FCSTD DOCUMENT  (FreeCAD 0.21R33771 (Git))
Label: Fiber_mount_assembly_Montana
License: All rights reserved
LicenseURL: https://en.wikipedia.org/wiki/All_rights_reserved
objects: App::Link×9, App::DocumentObjectGroup×2, PartDesign::CoordinateSystem×1, App::FeaturePython×1, App::Part×1
note: 1 computed .brp shape members not serialized (recipe doc carries the construction recipe); baked Part::Feature solids carry a one-line shape summary decoded from their .brp
EXTERNAL_REF file=../Optomecanics/Cage.FCStd obj=HoleAxis_1
EXTERNAL_REF file=Fiber_buffer_montana.FCStd obj=Top_center
EXTERNAL_REF file=../Optomecanics/Cage.FCStd obj=Assembly
EXTERNAL_REF file=../Optomecanics/Cage.FCStd obj=HoleAxis_3
EXTERNAL_REF file=../Optomecanics/Cage_rods.FCStd obj=HoleAxis_1
EXTERNAL_REF file=../Optomecanics/Cage_rods.FCStd obj=Assembly
EXTERNAL_REF file=../Optomecanics/Cage.FCStd obj=HoleAxis_4
EXTERNAL_REF file=../Optomecanics/Cage.FCStd obj=HoleAxis_5
EXTERNAL_REF file=../Optomecanics/Cage.FCStd obj=HoleAxis_6
EXTERNAL_REF file=../Optomecanics/Cage.FCStd obj=HoleAxis_2
EXTERNAL_REF file=SMA_port.FCStd obj=HoleAxis_1
EXTERNAL_REF file=SMA_port.FCStd obj=Assembly
EXTERNAL_REF file=Fiber_buffer_montana.FCStd obj=Bottom_center
EXTERNAL_REF file=../Optomecanics/Post_4inches.FCStd obj=HoleAxis_2
EXTERNAL_REF file=Fiber_buffer_montana.FCStd obj=Assembly
EXTERNAL_REF file=../Optomecanics/Post_4inches.FCStd obj=HoleAxis_1
EXTERNAL_REF file=../Optomecanics/Post_4inches.FCStd obj=Assembly

FEATURE [PartDesign::CoordinateSystem] LCS_Origin
  AttacherType = Attacher::AttachEngine3D
  MapMode = 2
  Support = -> [X_Axis]
FEATURE [App::DocumentObjectGroup] Constraints
FEATURE [App::FeaturePython] Variables  # WARN: FeaturePython — macro-defined, semantics opaque (R4)
  Type = App::PropertyContainer
FEATURE [App::DocumentObjectGroup] Configurations
FEATURE [App::Link] Cage
  AttachedBy = #HoleAxis_1
  AttachedTo = Fiber_buffer_montana#Top_center
  LinkPlacement = pos=(-1.35e-14,9.8e-15,141.92) rot=(0.57735,0.57735,0.57735;2.0944rad)
  LinkedObject = -> <external ../Optomecanics/Cage.FCStd>#Assembly
  Placement = pos=(-1.35e-14,9.8e-15,141.92) rot=(0.57735,0.57735,0.57735;2.0944rad)
  SolverId = Asm4EE
  expr: Placement = Fiber_buffer_montana.Placement * Fiber_buffer_montana#Top_center.Placement * AttachmentOffset * Cage#HoleAxis_1.Placement ^ -1
FEATURE [App::Link] Cage_rods  label="Cage_rod1"
  AttachedBy = #HoleAxis_1
  AttachedTo = Cage#HoleAxis_3
  AttachmentOffset = pos=(0,0,5) rot=(0,1,0;3.14159rad)
  LinkPlacement = pos=(20.527,-15,156.92) rot=(0.022572,-0.99949,-0.022572;1.57131rad)
  LinkedObject = -> <external ../Optomecanics/Cage_rods.FCStd>#Assembly
  Placement = pos=(20.527,-15,156.92) rot=(0.022572,-0.99949,-0.022572;1.57131rad)
  SolverId = Asm4EE
  expr: Placement = Cage.Placement * Cage#HoleAxis_3.Placement * AttachmentOffset * Cage_rods#HoleAxis_1.Placement ^ -1
FEATURE [App::Link] Cage_rods001  label="Cage_rod2"
  AttachedBy = #HoleAxis_1
  AttachedTo = Cage#HoleAxis_4
  AttachmentOffset = pos=(0,0,5) rot=(0,1,0;3.14159rad)
  LinkPlacement = pos=(20.527,15,156.92) rot=(0.022572,-0.99949,-0.022572;1.57131rad)
  LinkedObject = -> <external ../Optomecanics/Cage_rods.FCStd>#Assembly
  Placement = pos=(20.527,15,156.92) rot=(0.022572,-0.99949,-0.022572;1.57131rad)
  SolverId = Asm4EE
  expr: Placement = Cage.Placement * Cage#HoleAxis_4.Placement * AttachmentOffset * Cage_rods#HoleAxis_1.Placement ^ -1
FEATURE [App::Link] Cage_rods002  label="Cage_rod3"
  AttachedBy = #HoleAxis_1
  AttachedTo = Cage#HoleAxis_5
  AttachmentOffset = pos=(0,0,5) rot=(0,1,0;3.14159rad)
  LinkPlacement = pos=(20.527,-15,126.92) rot=(0.022572,-0.99949,-0.022572;1.57131rad)
  LinkedObject = -> <external ../Optomecanics/Cage_rods.FCStd>#Assembly
  Placement = pos=(20.527,-15,126.92) rot=(0.022572,-0.99949,-0.022572;1.57131rad)
  SolverId = Asm4EE
  expr: Placement = Cage.Placement * Cage#HoleAxis_5.Placement * AttachmentOffset * Cage_rods#HoleAxis_1.Placement ^ -1
FEATURE [App::Link] Cage_rods003  label="Cage_rod4"
  AttachedBy = #HoleAxis_1
  AttachedTo = Cage#HoleAxis_6
  AttachmentOffset = pos=(0,0,5) rot=(0.707107,0.707107,0;3.14159rad)
  LinkPlacement = pos=(20.527,15,126.92) rot=(0.585847,-0.55997,-0.585847;2.12066rad)
  LinkedObject = -> <external ../Optomecanics/Cage_rods.FCStd>#Assembly
  Placement = pos=(20.527,15,126.92) rot=(0.585847,-0.55997,-0.585847;2.12066rad)
  SolverId = Asm4EE
  expr: Placement = Cage.Placement * Cage#HoleAxis_6.Placement * AttachmentOffset * Cage_rods#HoleAxis_1.Placement ^ -1
FEATURE [App::Link] Cage001
  AttachedBy = #HoleAxis_2
  AttachedTo = Cage#HoleAxis_2
  AttachmentOffset = pos=(0,0,-35) rot=(0,0,1;0rad)
  LinkPlacement = pos=(35,-4.1e-15,141.92) rot=(0.57735,0.57735,0.57735;2.0944rad)
  LinkedObject = -> <external ../Optomecanics/Cage.FCStd>#Assembly
  Placement = pos=(35,-4.1e-15,141.92) rot=(0.57735,0.57735,0.57735;2.0944rad)
  SolverId = Asm4EE
  expr: Placement = Cage.Placement * Cage#HoleAxis_2.Placement * AttachmentOffset * Cage#HoleAxis_2.Placement ^ -1
FEATURE [App::Link] SMA_port
  AttachedBy = #HoleAxis_1
  AttachedTo = Cage001#HoleAxis_2
  AttachmentOffset = pos=(0,0,3) rot=(0,1,0;3.14159rad)
  LinkPlacement = pos=(39.62,-4.51e-14,141.92) rot=(1,0,0;4.71239rad)
  LinkedObject = -> <external SMA_port.FCStd>#Assembly
  Placement = pos=(39.62,-4.51e-14,141.92) rot=(1,0,0;4.71239rad)
  SolverId = Asm4EE
  expr: Placement = Cage001.Placement * Cage#HoleAxis_2.Placement * AttachmentOffset * SMA_port#HoleAxis_1.Placement ^ -1
FEATURE [App::Link] Fiber_buffer_montana
  AttachedBy = #Bottom_center
  AttachedTo = Post_4inches#HoleAxis_2
  LinkPlacement = pos=(-8.1e-15,5.7e-15,101.6) rot=(0,0,1;0rad)
  LinkedObject = -> <external Fiber_buffer_montana.FCStd>#Assembly
  Placement = pos=(-8.1e-15,5.7e-15,101.6) rot=(0,0,1;0rad)
  SolverId = Asm4EE
  expr: Placement = Post_4inches.Placement * Post_4inches#HoleAxis_2.Placement * AttachmentOffset * Fiber_buffer_montana#Bottom_center.Placement ^ -1
FEATURE [App::Link] Post_4inches
  AttachedBy = #HoleAxis_1
  AttachedTo = Parent Assembly#LCS_Origin
  LinkPlacement = pos=(-5.3e-15,-1.07e-14,50.8) rot=(0.57735,0.57735,0.57735;2.0944rad)
  LinkedObject = -> <external ../Optomecanics/Post_4inches.FCStd>#Assembly
  Placement = pos=(-5.3e-15,-1.07e-14,50.8) rot=(0.57735,0.57735,0.57735;2.0944rad)
  SolverId = Asm4EE
  expr: Placement = LCS_Origin.Placement * AttachmentOffset * Post_4inches#HoleAxis_1.Placement ^ -1
FEATURE [App::Part] Assembly
  AssemblyType = Part::Link
  Group = -> [LCS_Origin,Constraints,Variables,Configurations,Cage,Cage_rods,Cage_rods001,Cage_rods002,Cage_rods003,Cage001,SMA_port,Fiber_buffer_montana,Post_4inches]
  Origin = -> Origin
  Type = Assembly

RESOLVED EXTERNAL PARTS (link-assembly join: the EXTERNAL_REF files above that resolve inside this repo's crawl, each included once):
---- part Fiber_buffer_montana.FCStd = doc fcstd_8a898043692d ----
FCSTD DOCUMENT  (FreeCAD 0.21R33771 (Git))
Label: Fiber_buffer_montana
License: All rights reserved
LicenseURL: https://en.wikipedia.org/wiki/All_rights_reserved
objects: Sketcher::SketchObject×2, App::DocumentObjectGroup×2, PartDesign::CoordinateSystem×2, PartDesign::Pad×1, PartDesign::Hole×1, PartDesign::Body×1, App::FeaturePython×1, App::Part×1
note: 9 computed .brp shape members not serialized (recipe doc carries the construction recipe); baked Part::Feature solids carry a one-line shape summary decoded from their .brp

FEATURE [Sketcher::SketchObject] Sketch
  FullyConstrained = true
  MapMode = 5
  Support = -> [XY_Plane]
  sketch-geometry (4):
    g0: LineSegment StartX=-12.7 StartY=12.7 StartZ=0 EndX=12.7 EndY=12.7 EndZ=0
    g1: LineSegment StartX=12.7 StartY=12.7 StartZ=0 EndX=12.7 EndY=-12.7 EndZ=0
    g2: LineSegment StartX=12.7 StartY=-12.7 StartZ=0 EndX=-12.7 EndY=-12.7 EndZ=0
    g3: LineSegment StartX=-12.7 StartY=-12.7 StartZ=0 EndX=-12.7 EndY=12.7 EndZ=0
  constraints (12):
    c: Coincident(g0,g1)
    c: Coincident(g1,g2)
    c: Coincident(g2,g3)
    c: Coincident(g3,g0)
    c: Horizontal(g0)
    c: Horizontal(g2)
    c: Vertical(g1)
    c: Vertical(g3)
    c: DistanceX(g0,g-1) = 12.7
    c: DistanceX(g0,g0) = 25.4
    c: DistanceY(g1,g1) = 25.4
    c: DistanceY(g1,g-1) = 12.7
FEATURE [PartDesign::Pad] Pad
  Direction = (0,0,1)
  Length = 20
  Length2 = 10
  Profile = -> Sketch
  ReferenceAxis = -> Sketch [N_Axis]
  Type = 0
FEATURE [Sketcher::SketchObject] Sketch001
  FullyConstrained = true
  MapMode = 5
  Placement = pos=(0,0,20) rot=(0,0,1;0rad)
  Support = -> [Pad]
  sketch-geometry (1):
    g0: Circle CenterX=0 CenterY=0 CenterZ=0 NormalX=0 NormalY=0 NormalZ=1 AngleXU=0 Radius=1.5875
  constraints (2):
    c: Coincident(g0,g-1)
    c: Diameter(g0) = 3.175
FEATURE [PartDesign::Hole] Hole
  BaseFeature = -> Pad
  CustomThreadClearance = 0
  Depth = 75.3197
  DepthType = 1
  Diameter = 3.17
  DrillForDepth = false
  DrillPoint = 1
  DrillPointAngle = 118
  HoleCutCountersinkAngle = 90
  HoleCutCustomValues = false
  HoleCutDepth = 0
  HoleCutDiameter = 6.1
  HoleCutType = 0
  ModelThread = false
  Profile = -> Sketch001
  Tapered = false
  TaperedAngle = 90
  ThreadClass = 0
  ThreadDepth = 75.3197
  ThreadDepthType = 0
  ThreadDirection = 0
  ThreadFit = 0
  ThreadSize = 0
  ThreadType = 0
  Threaded = false
  UseCustomThreadClearance = false
FEATURE [PartDesign::Body] Body
  Group = -> [Sketch,Pad,Sketch001,Hole]
  Origin = -> Origin
  Tip = -> Hole
FEATURE [App::DocumentObjectGroup] Constraints
FEATURE [App::FeaturePython] Variables  # WARN: FeaturePython — macro-defined, semantics opaque (R4)
  Type = App::PropertyContainer
FEATURE [App::DocumentObjectGroup] Configurations
FEATURE [PartDesign::CoordinateSystem] Bottom_center
  AttacherType = Attacher::AttachEngine3D
FEATURE [PartDesign::CoordinateSystem] Top_center
  AttacherType = Attacher::AttachEngine3D
  Placement = pos=(0,0,20) rot=(0,0,1;0rad)
FEATURE [App::Part] Assembly
  AssemblyType = Part::Link
  Group = -> [Constraints,Variables,Configurations,Body,Bottom_center,Top_center]
  Origin = -> Origin001
  Type = Assembly
